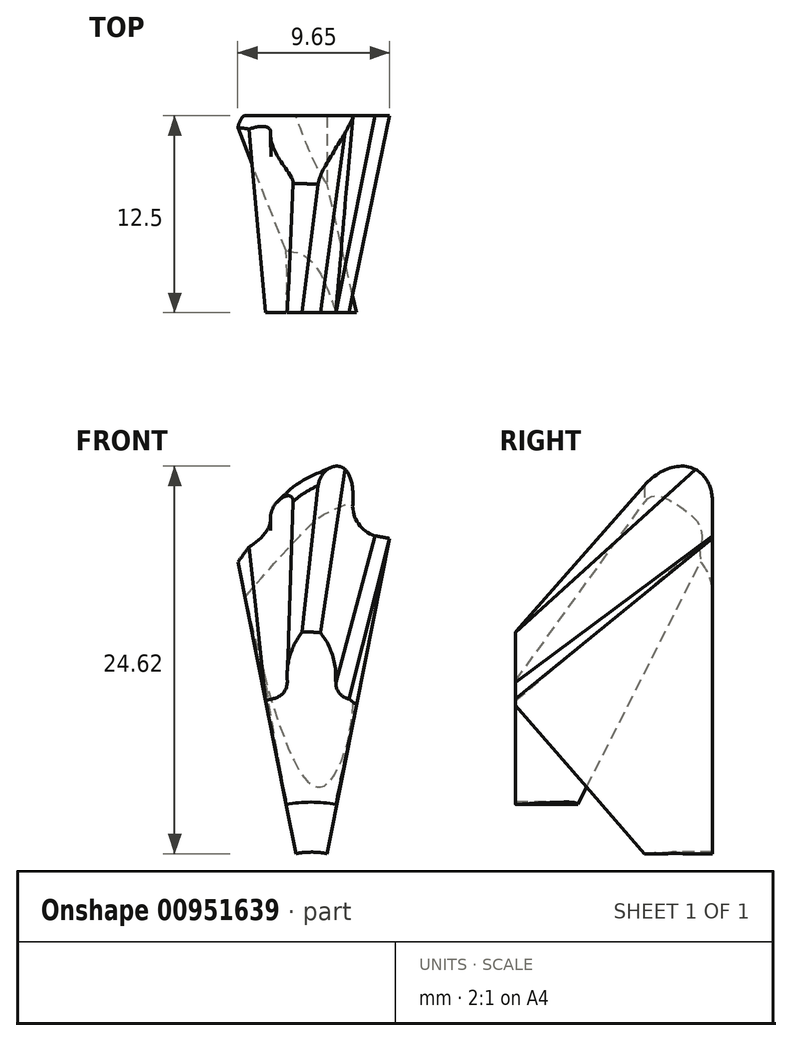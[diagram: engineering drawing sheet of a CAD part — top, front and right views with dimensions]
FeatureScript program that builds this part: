
annotation { "Feature Type Name" : "Feature", "Feature Type Description" : "" }
export const myFeature = defineFeature(function(context is Context, id is Id, definition is map)
    precondition{}
    {
        {
            var Q0;
            Q0=qCreatedBy(makeId("Front.planeOp"),FACE);
            cPlane(context, id + "F0", {"entities" : qUnion([Q0]), "cplaneType" : CPlaneType.OFFSET, "offset" : 12.7 * mm, "oppositeDirection" : true, "width" : 152.4 * mm, "height" : 152.4 * mm});
        }
        {
            assignVariable(context, id + "F1", {"name" : "GearThickness", "anyValue" : .1});
        }
        {
            var Q0;
            Q0=qCreatedBy(makeId("Front.planeOp"),FACE);
            var sketch = newSketch(context, id + "F2", { "sketchPlane" : qUnion([Q0])});
            skCircle(sketch, "E0", {"center": v(0, 0) * mm, "radius": 14.88 * mm});
            skSolve(sketch);
        }
        {
            var Q0;
            Q0=qSketchRegion(id+"F2",true);
            extrude(context, id + "F3", {"entities" : qUnion([Q0]), "endBound" : BoundingType.SYMMETRIC, "offsetDistance" : 25 * mm, "depth" : (getVariable(context, 'GearThickness')) * mm});
        }
        {
            var Q0;
            Q0=qCreatedBy(makeId("Front.planeOp"),FACE);
            var sketch = newSketch(context, id + "F4", { "sketchPlane" : qUnion([Q0])});
            skCircle(sketch, "E1", {"center": v(0, 0) * mm, "radius": 16.88 * mm, "construction": true});
            skLineSegment(sketch, "E2", {"start": v(0, 28.09) * mm, "end": v(0, 0) * mm, "construction": true});
            skLineSegment(sketch, "E3", {"start": v(0, 0) * mm, "end": v(-1.47, 16.81) * mm, "construction": true});
            skLineSegment(sketch, "E4", {"start": v(0, 0) * mm, "end": v(1.47, 16.81) * mm, "construction": true});
            skCircle(sketch, "E5", {"center": v(0, 0) * mm, "radius": 18.88 * mm, "construction": true});
            skArc(sketch, "E6", {"start": v(1.35, 14.81) * mm, "mid": v(0, 14.88) * mm, "end": v(-1.35, 14.81) * mm});
            skArc(sketch, "E7", {"start": v(0.55, 18.87) * mm, "mid": v(0, 18.88) * mm, "end": v(-0.55, 18.87) * mm});
            skLineSegment(sketch, "E8", {"start": v(-1.47, 16.81) * mm, "end": v(-1.27, 18.02) * mm, "construction": true});
            skLineSegment(sketch, "E9", {"start": v(-1.47, 16.81) * mm, "end": v(-0.55, 18.87) * mm, "construction": true});
            skArc(sketch, "E10", {"start": v(-0.55, 18.87) * mm, "mid": v(-1.45, 16.94) * mm, "end": v(-1.35, 14.81) * mm});
            skArc(sketch, "E11", {"start": v(1.35, 14.81) * mm, "mid": v(1.45, 16.94) * mm, "end": v(0.55, 18.87) * mm});
            skSolve(sketch);
        }
        {
            var Q0;
            Q0=qSketchRegion(id+"F4",true);
            extrude(context, id + "F5", {"entities" : qUnion([Q0]), "endBound" : BoundingType.SYMMETRIC, "depth" : (getVariable(context, 'GearThickness')) * mm});
        }
        {
            var Q0;
            Q0=qCreatedBy(makeId("Front.planeOp"),FACE);
            var sketch = newSketch(context, id + "F6", { "sketchPlane" : qUnion([Q0])});
            skArc(sketch, "E12", {"start": v(1.52, 15.75) * mm, "mid": v(1.73, 15.05) * mm, "end": v(2.36, 14.69) * mm});
            skArc(sketch, "E13", {"start": v(-2.36, 14.69) * mm, "mid": v(-1.73, 15.05) * mm, "end": v(-1.52, 15.75) * mm});
            skArc(sketch, "E14", {"start": v(2.36, 14.69) * mm, "mid": v(0, 14.88) * mm, "end": v(-2.36, 14.69) * mm});
            skLineSegment(sketch, "E15", {"start": v(-1.52, 15.75) * mm, "end": v(1.52, 15.75) * mm});
            skSolve(sketch);
        }
        {
            var Q0;
            Q0=qSketchRegion(id+"F6",true);
            extrude(context, id + "F7", {"entities" : qUnion([Q0]), "operationType" : NewBodyOperationType.ADD, "endBound" : BoundingType.SYMMETRIC, "offsetDistance" : 25.4 * mm, "depth" : (getVariable(context, 'GearThickness')) * mm});
        }
        {
            var Q0;
            Q0=makeQuery(id+"F3.opExtrude","CAP_FACE",FACE,{"disambiguationData":[OSD([sQuery(id+"F2.wireOp",EDGE,"E0")])],"isStart":true});
            var sketch = newSketch(context, id + "F8", { "sketchPlane" : qUnion([Q0])});
            skLineSegment(sketch, "E16", {"start": v(0, 0) * mm, "end": v(-2.36, 14.69) * mm, "construction": true});
            skLineSegment(sketch, "E17", {"start": v(0, 0) * mm, "end": v(-1.52, 15.75) * mm, "construction": true});
            skLineSegment(sketch, "E18", {"start": v(0, 0) * mm, "end": v(-0.55, 18.87) * mm, "construction": true});
            skLineSegment(sketch, "E19", {"start": v(0, 0) * mm, "end": v(0.55, 18.87) * mm, "construction": true});
            skLineSegment(sketch, "E20", {"start": v(0, 0) * mm, "end": v(1.52, 15.75) * mm, "construction": true});
            skLineSegment(sketch, "E21", {"start": v(0, 0) * mm, "end": v(2.36, 14.69) * mm, "construction": true});
            skSolve(sketch);
        }
        {
            var Q0;
            Q0=qCreatedBy(makeId("Top.planeOp"),FACE);
            var sketch = newSketch(context, id + "F9", { "sketchPlane" : qUnion([Q0])});
            skLineSegment(sketch, "E22", {"start": v(0, 0) * mm, "end": v(0, 9.45) * mm});
            skSolve(sketch);
        }
        {
            var Q0;
            Q0=sQuery(id+"F9.wireOp",VERTEX,"E22.end");
            var Q1;
            Q1=sQuery(id+"F9.wireOp",VERTEX,"E22.start");
            var Q2;
            Q2=sQuery(id+"F8.wireOp",VERTEX,"E16.end");
            cPlane(context, id + "F10", {"entities" : qUnion([Q0, Q1, Q2]), "cplaneType" : CPlaneType.THREE_POINT, "offset" : 25.4 * mm, "width" : 152.4 * mm, "height" : 152.4 * mm});
        }
        {
            var Q0;
            Q0=qCreatedBy(id+"F10.planeOp",FACE);
            var sketch = newSketch(context, id + "F11", { "sketchPlane" : qUnion([Q0])});
            skLineSegment(sketch, "E23", {"start": v(0.05, 14.88) * mm, "end": v(12.7, 27.53) * mm});
            skSolve(sketch);
        }
        {
            var Q0;
            Q0=sQuery(id+"F8.wireOp",VERTEX,"E20.start");
            var Q1;
            Q1=sQuery(id+"F9.wireOp",VERTEX,"E22.end");
            var Q2;
            Q2=sQuery(id+"F8.wireOp",VERTEX,"E17.end");
            cPlane(context, id + "F12", {"entities" : qUnion([Q0, Q1, Q2]), "cplaneType" : CPlaneType.THREE_POINT, "offset" : 25.4 * mm, "width" : 152.4 * mm, "height" : 152.4 * mm});
        }
        {
            var Q0;
            Q0=qCreatedBy(id+"F12.planeOp",FACE);
            var sketch = newSketch(context, id + "F13", { "sketchPlane" : qUnion([Q0])});
            skLineSegment(sketch, "E24", {"start": v(-0.05, 15.82) * mm, "end": v(-12.7, 28.47) * mm});
            skSolve(sketch);
        }
        {
            var Q0;
            Q0=sQuery(id+"F8.wireOp",VERTEX,"E18.end");
            var Q1;
            Q1=sQuery(id+"F9.wireOp",VERTEX,"E22.end");
            var Q2;
            Q2=sQuery(id+"F9.wireOp",VERTEX,"E22.start");
            cPlane(context, id + "F14", {"entities" : qUnion([Q0, Q1, Q2]), "cplaneType" : CPlaneType.THREE_POINT, "offset" : 25.4 * mm, "width" : 152.4 * mm, "height" : 152.4 * mm});
        }
        {
            var Q0;
            Q0=qCreatedBy(id+"F14.planeOp",FACE);
            var sketch = newSketch(context, id + "F15", { "sketchPlane" : qUnion([Q0])});
            skLineSegment(sketch, "E25", {"start": v(0.05, 18.88) * mm, "end": v(12.7, 31.53) * mm});
            skSolve(sketch);
        }
        {
            var Q0;
            Q0=sQuery(id+"F8.wireOp",VERTEX,"E20.start");
            var Q1;
            Q1=sQuery(id+"F8.wireOp",VERTEX,"E19.end");
            var Q2;
            Q2=sQuery(id+"F9.wireOp",VERTEX,"E22.end");
            cPlane(context, id + "F16", {"entities" : qUnion([Q0, Q1, Q2]), "cplaneType" : CPlaneType.THREE_POINT, "offset" : 25.4 * mm, "width" : 152.4 * mm, "height" : 152.4 * mm});
        }
        {
            var Q0;
            Q0=qCreatedBy(id+"F16.planeOp",FACE);
            var sketch = newSketch(context, id + "F17", { "sketchPlane" : qUnion([Q0])});
            skLineSegment(sketch, "E26", {"start": v(0.05, 18.88) * mm, "end": v(12.7, 31.53) * mm});
            skSolve(sketch);
        }
        {
            var Q0;
            Q0=sQuery(id+"F9.wireOp",VERTEX,"E22.end");
            var Q1;
            Q1=sQuery(id+"F9.wireOp",VERTEX,"E22.start");
            var Q2;
            Q2=sQuery(id+"F8.wireOp",VERTEX,"E20.end");
            cPlane(context, id + "F18", {"entities" : qUnion([Q0, Q1, Q2]), "cplaneType" : CPlaneType.THREE_POINT, "offset" : 25.4 * mm, "width" : 152.4 * mm, "height" : 152.4 * mm});
        }
        {
            var Q0;
            Q0=qCreatedBy(id+"F18.planeOp",FACE);
            var sketch = newSketch(context, id + "F19", { "sketchPlane" : qUnion([Q0])});
            skLineSegment(sketch, "E27", {"start": v(0.05, 15.82) * mm, "end": v(12.7, 28.47) * mm});
            skSolve(sketch);
        }
        {
            var Q0;
            Q0=sQuery(id+"F9.wireOp",VERTEX,"E22.end");
            var Q1;
            Q1=sQuery(id+"F8.wireOp",VERTEX,"E21.end");
            var Q2;
            Q2=sQuery(id+"F9.wireOp",VERTEX,"E22.start");
            cPlane(context, id + "F20", {"entities" : qUnion([Q0, Q1, Q2]), "cplaneType" : CPlaneType.THREE_POINT, "offset" : 25.4 * mm, "width" : 152.4 * mm, "height" : 152.4 * mm});
        }
        {
            var Q0;
            Q0=qCreatedBy(id+"F20.planeOp",FACE);
            var sketch = newSketch(context, id + "F21", { "sketchPlane" : qUnion([Q0])});
            skLineSegment(sketch, "E28", {"start": v(-0.05, 14.88) * mm, "end": v(-12.7, 27.53) * mm});
            skSolve(sketch);
        }
        {
            var Q0;
            Q0=qCreatedBy(id+"F0.planeOp",FACE);
            var sketch = newSketch(context, id + "F22", { "sketchPlane" : qUnion([Q0])});
            skArc(sketch, "E29", {"start": v(0.98, 33.3) * mm, "mid": v(0, 33.3) * mm, "end": v(-0.98, 33.3) * mm});
            skArc(sketch, "E30", {"start": v(-0.98, 33.3) * mm, "mid": v(-2.28, 30.38) * mm, "end": v(-2.62, 27.2) * mm});
            skArc(sketch, "E31", {"start": v(2.62, 27.2) * mm, "mid": v(2.28, 30.38) * mm, "end": v(0.98, 33.3) * mm});
            skArc(sketch, "E32", {"start": v(-4.04, 25.17) * mm, "mid": v(-2.98, 25.94) * mm, "end": v(-2.62, 27.2) * mm});
            skArc(sketch, "E33", {"start": v(2.62, 27.2) * mm, "mid": v(2.98, 25.94) * mm, "end": v(4.04, 25.17) * mm});
            skLineSegment(sketch, "E34", {"start": v(0, 0) * mm, "end": v(-4.04, 25.17) * mm, "construction": true});
            skLineSegment(sketch, "E35", {"start": v(0, 0) * mm, "end": v(-2.62, 27.2) * mm, "construction": true});
            skLineSegment(sketch, "E36", {"start": v(0, 0) * mm, "end": v(-0.98, 33.3) * mm, "construction": true});
            skLineSegment(sketch, "E37", {"start": v(0, 0) * mm, "end": v(0.98, 33.3) * mm, "construction": true});
            skLineSegment(sketch, "E38", {"start": v(0, 0) * mm, "end": v(2.62, 27.2) * mm, "construction": true});
            skLineSegment(sketch, "E39", {"start": v(0, 0) * mm, "end": v(4.04, 25.17) * mm, "construction": true});
            skLineSegment(sketch, "E40", {"start": v(0, 0) * mm, "end": v(4.97, 25) * mm});
            skLineSegment(sketch, "E41", {"start": v(0, 0) * mm, "end": v(-4.97, 25) * mm});
            skLineSegment(sketch, "E42", {"start": v(0, 0) * mm, "end": v(0, 20.32) * mm, "construction": true});
            skArc(sketch, "E43", {"start": v(-4.04, 25.17) * mm, "mid": v(-4.5, 25.09) * mm, "end": v(-4.97, 25) * mm});
            skArc(sketch, "E44", {"start": v(4.97, 25) * mm, "mid": v(4.5, 25.09) * mm, "end": v(4.04, 25.17) * mm});
            skSolve(sketch);
        }
        {
            var Q0;
            Q0=makeQuery(id+"F8.imprint","IMPRINT",FACE,{"disambiguationData":[TD([[makeQuery(id+"F8.imprint","IMPRINT",EDGE,{"derivedFrom":makeQuery(id+"F3.opExtrude","CAP_EDGE",EDGE,{"disambiguationData":[OSD([sQuery(id+"F2.wireOp",EDGE,"E0")])],"isStart":true})}),-1.0]])]});
            var sketch = newSketch(context, id + "F23", { "sketchPlane" : qUnion([Q0])});
            skLineSegment(sketch, "E45", {"start": v(0, 0) * mm, "end": v(-2.36, 14.69) * mm, "construction": true});
            skLineSegment(sketch, "E46", {"start": v(0, 0) * mm, "end": v(2.36, 14.69) * mm, "construction": true});
            skArc(sketch, "E47.0", {"start": v(-1.52, 15.76) * mm, "mid": v(-1.73, 15.06) * mm, "end": v(-2.36, 14.69) * mm});
            skArc(sketch, "E47.1", {"start": v(2.36, 14.69) * mm, "mid": v(1.74, 15.06) * mm, "end": v(1.54, 15.75) * mm});
            skArc(sketch, "E47.2", {"start": v(0.61, 18.89) * mm, "mid": v(1.37, 17.4) * mm, "end": v(1.54, 15.75) * mm});
            skArc(sketch, "E47.3", {"start": v(-0.54, 18.89) * mm, "mid": v(0.03, 18.9) * mm, "end": v(0.61, 18.89) * mm});
            skArc(sketch, "E47.4", {"start": v(-1.52, 15.76) * mm, "mid": v(-1.33, 17.41) * mm, "end": v(-0.54, 18.89) * mm});
            skLineSegment(sketch, "E48", {"start": v(0, 0) * mm, "end": v(-2.9, 14.59) * mm});
            skLineSegment(sketch, "E49", {"start": v(0, 0) * mm, "end": v(2.9, 14.59) * mm});
            skLineSegment(sketch, "E50", {"start": v(0, 0) * mm, "end": v(0, 6.32) * mm});
            skArc(sketch, "E51", {"start": v(-2.36, 14.69) * mm, "mid": v(-2.63, 14.64) * mm, "end": v(-2.9, 14.59) * mm});
            skArc(sketch, "E52", {"start": v(2.9, 14.59) * mm, "mid": v(2.63, 14.64) * mm, "end": v(2.36, 14.69) * mm});
            skSolve(sketch);
        }
        {
            var Q0;
            Q0=qSketchRegion(id+"F23",true);
            var Q1;
            Q1=qSketchRegion(id+"F22",true);
            loft(context, id + "F24", {"sheetProfilesArray" : [{ "sheetProfileEntities" : qUnion([Q0]) }, { "sheetProfileEntities" : qUnion([Q1]) }]});
        }
        {
            var Q0;
            Q0=makeQuery(id+"F24.opLoft","MID_CAP_EDGE",EDGE,{"disambiguationData":[OSD([sQuery(id+"F22.wireOp",EDGE,"E29"),sQuery(id+"F22.wireOp",EDGE,"E30"),sQuery(id+"F22.wireOp",EDGE,"E31")])],"capPos":1.0});
            fillet(context, id + "F25", {"entities" : qUnion([Q0]), "radius" : 2.54 * mm, "tangentPropagation" : true, "allowEdgeOverflow" : false});
        }
        {
            var Q0;
            Q0=makeQuery(id+"F1nLDo3oGZqNCE5_2.boolean.opBoolean","MERGE",FACE,{"derivedFrom":[makeQuery(id+"F3.opExtrude","CAP_FACE",FACE,{"disambiguationData":[OSD([sQuery(id+"F2.wireOp",EDGE,"E0")])],"isStart":false}),makeQuery(id+"F7.boolean.opBoolean","MERGE",FACE,{"derivedFrom":[makeQuery(id+"F5.opExtrude","CAP_FACE",FACE,{"disambiguationData":[OSD([sQuery(id+"F4.wireOp",EDGE,"E6"),sQuery(id+"F4.wireOp",EDGE,"E7"),sQuery(id+"F4.wireOp",EDGE,"E10"),sQuery(id+"F4.wireOp",EDGE,"E11")])],"isStart":false}),makeQuery(id+"F7.opExtrude","CAP_FACE",FACE,{"disambiguationData":[OSD([sQuery(id+"F6.wireOp",EDGE,"E12"),sQuery(id+"F6.wireOp",EDGE,"E13"),sQuery(id+"F6.wireOp",EDGE,"E14"),sQuery(id+"F6.wireOp",EDGE,"E15")])],"isStart":false})]})]});
            var sketch = newSketch(context, id + "F26", { "sketchPlane" : qUnion([Q0])});
            skCircle(sketch, "E53", {"center": v(0, 0) * mm, "radius": 5.08 * mm});
            skSolve(sketch);
        }
        {
            var Q0;
            Q0=qSketchRegion(id+"F26",true);
            extrude(context, id + "F27", {"entities" : qUnion([Q0]), "operationType" : NewBodyOperationType.REMOVE, "endBound" : BoundingType.THROUGH_ALL, "oppositeDirection" : true, "depth" : 25.4 * mm, "offsetDistance" : 25.4 * mm});
        }
        {
            var Q0;
            Q0=makeQuery(id+"F24.boolean.opBoolean","MERGE",FACE,{"derivedFrom":[makeQuery(id+"F3.opExtrude","CAP_FACE",FACE,{"disambiguationData":[OSD([sQuery(id+"F2.wireOp",EDGE,"E0")])],"isStart":false}),makeQuery(id+"F7.boolean.opBoolean","MERGE",FACE,{"derivedFrom":[makeQuery(id+"F5.opExtrude","CAP_FACE",FACE,{"disambiguationData":[OSD([sQuery(id+"F4.wireOp",EDGE,"E6"),sQuery(id+"F4.wireOp",EDGE,"E7"),sQuery(id+"F4.wireOp",EDGE,"E10"),sQuery(id+"F4.wireOp",EDGE,"E11")])],"isStart":false}),makeQuery(id+"F7.opExtrude","CAP_FACE",FACE,{"disambiguationData":[OSD([sQuery(id+"F6.wireOp",EDGE,"E12"),sQuery(id+"F6.wireOp",EDGE,"E13"),sQuery(id+"F6.wireOp",EDGE,"E14"),sQuery(id+"F6.wireOp",EDGE,"E15")])],"isStart":false})]})]});
            var sketch = newSketch(context, id + "F28", { "sketchPlane" : qUnion([Q0])});
            skCircle(sketch, "E54", {"center": v(0, 0) * mm, "radius": 38.1 * mm});
            skSolve(sketch);
        }
        {
            var Q0;
            Q0=qSketchRegion(id+"F28",true);
            extrude(context, id + "F29", {"entities" : qUnion([Q0]), "operationType" : NewBodyOperationType.REMOVE, "oppositeDirection" : true, "depth" : 0.25 * mm, "offsetDistance" : 25.4 * mm});
        }
        {
            var Q0;
            {var subQ1=sQuery(id+"F23.wireOp",EDGE,"E47.2");var subQ5=sQuery(id+"F22.wireOp",EDGE,"E30");var subQ7=sQuery(id+"F23.wireOp",EDGE,"E47.3");var subQ8=sQuery(id+"F22.wireOp",EDGE,"E29");var subQ9=sQuery(id+"F23.wireOp",EDGE,"E47.4");var subQ12=sQuery(id+"F22.wireOp",EDGE,"E31");Q0=makeQuery(id+"F29.boolean.opBoolean","COPY",FACE,{"disambiguationData":[TD([makeQuery(id+"F6gZBTzl9evnY3P_3.1.F24.opLoft","SWEPT_FACE",FACE,{"disambiguationData":[OSD([subQ8,subQ5,subQ12,subQ1,subQ7,subQ9])]})])],"derivedFrom":makeQuery(id+"F29.opExtrude","CAP_FACE",FACE,{"disambiguationData":[OSD([sQuery(id+"F28.wireOp",EDGE,"E54")])],"isStart":false})});}
            var sketch = newSketch(context, id + "F30", { "sketchPlane" : qUnion([Q0])});
            skCircle(sketch, "E55", {"center": v(0, 0) * mm, "radius": 5.08 * mm});
            skCircle(sketch, "E56", {"center": v(0, 0) * mm, "radius": 6.48 * mm});
            skSolve(sketch);
        }
        {
            var Q0;
            Q0=qSketchRegion(id+"F30",true);
            extrude(context, id + "F31", {"entities" : qUnion([Q0]), "operationType" : NewBodyOperationType.ADD, "oppositeDirection" : true, "depth" : 2.54 * mm, "offsetDistance" : 25.4 * mm});
        }
        {
            var Q0;
            {var subQ1=sQuery(id+"F23.wireOp",EDGE,"E47.2");var subQ5=sQuery(id+"F22.wireOp",EDGE,"E30");var subQ7=sQuery(id+"F23.wireOp",EDGE,"E47.3");var subQ8=sQuery(id+"F22.wireOp",EDGE,"E29");var subQ9=sQuery(id+"F23.wireOp",EDGE,"E47.4");var subQ12=sQuery(id+"F22.wireOp",EDGE,"E31");var subQ27=makeQuery(id+"F29.opExtrude","CAP_FACE",FACE,{"disambiguationData":[OSD([sQuery(id+"F28.wireOp",EDGE,"E54")])],"isStart":false});Q0=makeQuery(id+"F31.boolean.opBoolean","MERGE",FACE,{"derivedFrom":[makeQuery(id+"F29.boolean.opBoolean","COPY",FACE,{"disambiguationData":[TD([makeQuery(id+"F24.opLoft","SWEPT_FACE",FACE,{"disambiguationData":[OSD([subQ8,subQ5,subQ12,subQ1,subQ7,subQ9])]})])],"derivedFrom":subQ27}),makeQuery(id+"F29.boolean.opBoolean","COPY",FACE,{"disambiguationData":[TD([makeQuery(id+"F6gZBTzl9evnY3P_3.1.F24.opLoft","SWEPT_FACE",FACE,{"disambiguationData":[OSD([subQ8,subQ5,subQ12,subQ1,subQ7,subQ9])]})])],"derivedFrom":subQ27}),makeQuery(id+"F29.boolean.opBoolean","COPY",FACE,{"disambiguationData":[TD([makeQuery(id+"F6gZBTzl9evnY3P_3.2.F24.opLoft","SWEPT_FACE",FACE,{"disambiguationData":[OSD([subQ8,subQ5,subQ12,subQ1,subQ7,subQ9])]})])],"derivedFrom":subQ27}),makeQuery(id+"F29.boolean.opBoolean","COPY",FACE,{"disambiguationData":[TD([makeQuery(id+"F6gZBTzl9evnY3P_3.3.F24.opLoft","SWEPT_FACE",FACE,{"disambiguationData":[OSD([subQ8,subQ5,subQ12,subQ1,subQ7,subQ9])]})])],"derivedFrom":subQ27}),makeQuery(id+"F29.boolean.opBoolean","COPY",FACE,{"disambiguationData":[TD([makeQuery(id+"F6gZBTzl9evnY3P_3.4.F24.opLoft","SWEPT_FACE",FACE,{"disambiguationData":[OSD([subQ8,subQ5,subQ12,subQ1,subQ7,subQ9])]})])],"derivedFrom":subQ27}),makeQuery(id+"F29.boolean.opBoolean","COPY",FACE,{"disambiguationData":[TD([makeQuery(id+"F6gZBTzl9evnY3P_3.5.F24.opLoft","SWEPT_FACE",FACE,{"disambiguationData":[OSD([subQ8,subQ5,subQ12,subQ1,subQ7,subQ9])]})])],"derivedFrom":subQ27}),makeQuery(id+"F29.boolean.opBoolean","COPY",FACE,{"disambiguationData":[TD([makeQuery(id+"F6gZBTzl9evnY3P_3.6.F24.opLoft","SWEPT_FACE",FACE,{"disambiguationData":[OSD([subQ8,subQ5,subQ12,subQ1,subQ7,subQ9])]})])],"derivedFrom":subQ27}),makeQuery(id+"F29.boolean.opBoolean","COPY",FACE,{"disambiguationData":[TD([makeQuery(id+"F6gZBTzl9evnY3P_3.7.F24.opLoft","SWEPT_FACE",FACE,{"disambiguationData":[OSD([subQ8,subQ5,subQ12,subQ1,subQ7,subQ9])]})])],"derivedFrom":subQ27}),makeQuery(id+"F29.boolean.opBoolean","COPY",FACE,{"disambiguationData":[TD([makeQuery(id+"F6gZBTzl9evnY3P_3.8.F24.opLoft","SWEPT_FACE",FACE,{"disambiguationData":[OSD([subQ8,subQ5,subQ12,subQ1,subQ7,subQ9])]})])],"derivedFrom":subQ27}),makeQuery(id+"F29.boolean.opBoolean","COPY",FACE,{"disambiguationData":[TD([makeQuery(id+"F6gZBTzl9evnY3P_3.9.F24.opLoft","SWEPT_FACE",FACE,{"disambiguationData":[OSD([subQ8,subQ5,subQ12,subQ1,subQ7,subQ9])]})])],"derivedFrom":subQ27}),makeQuery(id+"F29.boolean.opBoolean","COPY",FACE,{"disambiguationData":[TD([makeQuery(id+"F6gZBTzl9evnY3P_3.10.F24.opLoft","SWEPT_FACE",FACE,{"disambiguationData":[OSD([subQ8,subQ5,subQ12,subQ1,subQ7,subQ9])]})])],"derivedFrom":subQ27}),makeQuery(id+"F29.boolean.opBoolean","COPY",FACE,{"disambiguationData":[TD([makeQuery(id+"F6gZBTzl9evnY3P_3.11.F24.opLoft","SWEPT_FACE",FACE,{"disambiguationData":[OSD([subQ8,subQ5,subQ12,subQ1,subQ7,subQ9])]})])],"derivedFrom":subQ27}),makeQuery(id+"F29.boolean.opBoolean","COPY",FACE,{"disambiguationData":[TD([makeQuery(id+"F6gZBTzl9evnY3P_3.12.F24.opLoft","SWEPT_FACE",FACE,{"disambiguationData":[OSD([subQ8,subQ5,subQ12,subQ1,subQ7,subQ9])]})])],"derivedFrom":subQ27}),makeQuery(id+"F29.boolean.opBoolean","COPY",FACE,{"disambiguationData":[TD([makeQuery(id+"F6gZBTzl9evnY3P_3.13.F24.opLoft","SWEPT_FACE",FACE,{"disambiguationData":[OSD([subQ8,subQ5,subQ12,subQ1,subQ7,subQ9])]})])],"derivedFrom":subQ27}),makeQuery(id+"F29.boolean.opBoolean","COPY",FACE,{"disambiguationData":[TD([makeQuery(id+"F6gZBTzl9evnY3P_3.14.F24.opLoft","SWEPT_FACE",FACE,{"disambiguationData":[OSD([subQ8,subQ5,subQ12,subQ1,subQ7,subQ9])]})])],"derivedFrom":subQ27}),makeQuery(id+"F29.boolean.opBoolean","COPY",FACE,{"disambiguationData":[TD([makeQuery(id+"F6gZBTzl9evnY3P_3.15.F24.opLoft","SWEPT_FACE",FACE,{"disambiguationData":[OSD([subQ8,subQ5,subQ12,subQ1,subQ7,subQ9])]})])],"derivedFrom":subQ27}),makeQuery(id+"F29.boolean.opBoolean","COPY",FACE,{"disambiguationData":[TD([makeQuery(id+"F6gZBTzl9evnY3P_3.16.F24.opLoft","SWEPT_FACE",FACE,{"disambiguationData":[OSD([subQ8,subQ5,subQ12,subQ1,subQ7,subQ9])]})])],"derivedFrom":subQ27}),makeQuery(id+"F29.boolean.opBoolean","COPY",FACE,{"disambiguationData":[TD([makeQuery(id+"F6gZBTzl9evnY3P_3.17.F24.opLoft","SWEPT_FACE",FACE,{"disambiguationData":[OSD([subQ8,subQ5,subQ12,subQ1,subQ7,subQ9])]})])],"derivedFrom":subQ27}),makeQuery(id+"F31.opExtrude","CAP_FACE",FACE,{"disambiguationData":[OSD([sQuery(id+"F30.wireOp",EDGE,"E55"),sQuery(id+"F30.wireOp",EDGE,"E56")])],"isStart":true})]});}
            var sketch = newSketch(context, id + "F32", { "sketchPlane" : qUnion([Q0])});
            skCircle(sketch, "E57", {"center": v(0, 0) * mm, "radius": 8.26 * mm});
            skSolve(sketch);
        }
        {
            var Q0;
            Q0 = qSketchRegion(id + "F32", true);
            extrude(context, id + "F33", {"entities" : qUnion([Q0]), "operationType" : NewBodyOperationType.REMOVE, "oppositeDirection" : true, "depth" : 5.08 * mm, "offsetDistance" : 25.4 * mm});
        }
    });
